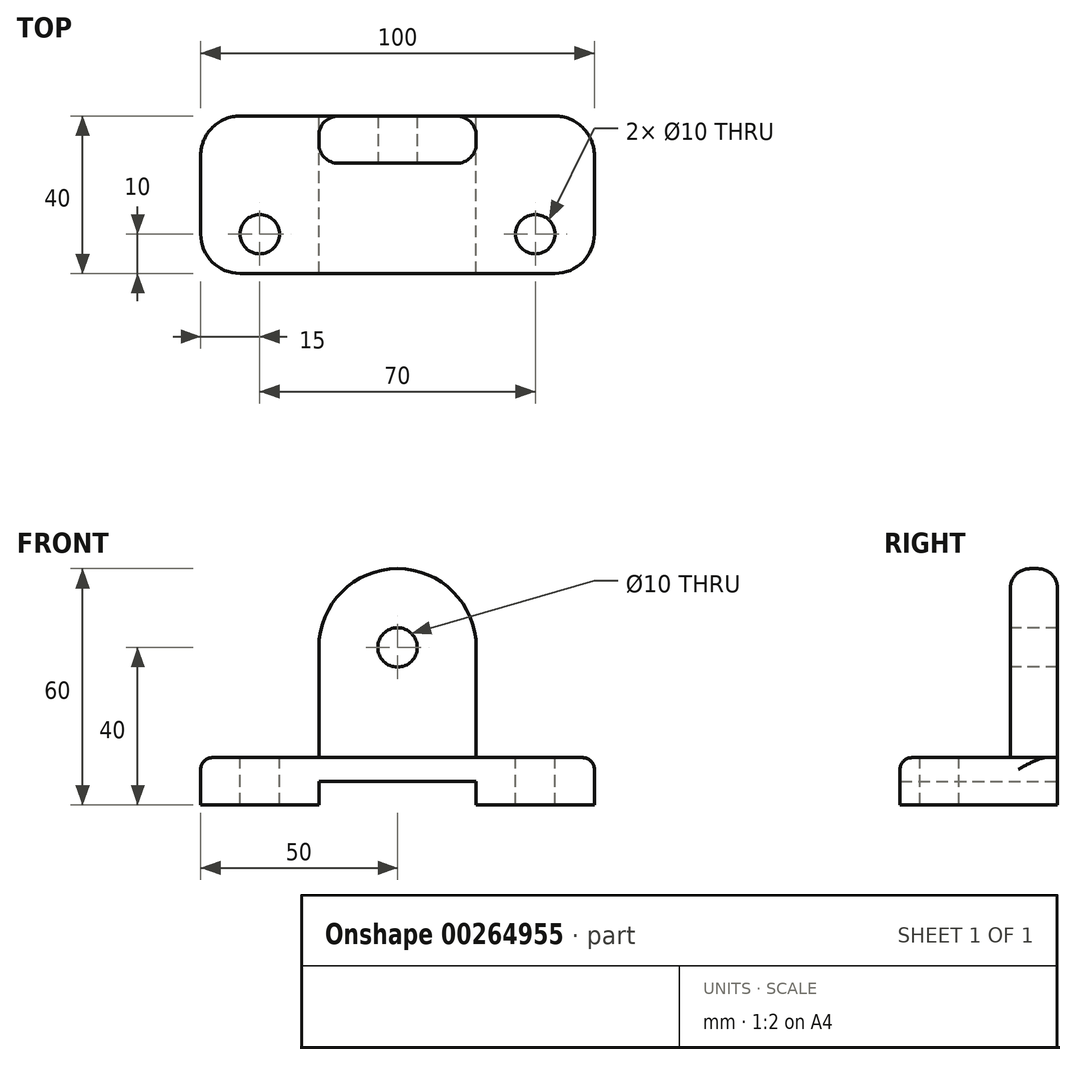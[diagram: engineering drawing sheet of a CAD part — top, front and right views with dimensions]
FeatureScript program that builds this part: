
annotation { "Feature Type Name" : "Feature", "Feature Type Description" : "" }
export const myFeature = defineFeature(function(context is Context, id is Id, definition is map)
    precondition{}
    {
        {
            var Q0;
            Q0=qCreatedBy(makeId("Top.planeOp"),FACE);
            var sketch = newSketch(context, id + "F0", { "sketchPlane" : qUnion([Q0])});
            skLineSegment(sketch, "E0.bottom", {"start": v(40, 20) * mm, "end": v(-40, 20) * mm});
            skLineSegment(sketch, "E0.top", {"start": v(40, -20) * mm, "end": v(-40, -20) * mm});
            skLineSegment(sketch, "E0.left", {"start": v(50, 10) * mm, "end": v(50, -10) * mm});
            skLineSegment(sketch, "E0.right", {"start": v(-50, 10) * mm, "end": v(-50, -10) * mm});
            skPoint(sketch, "E0.middle", {"position": v(0, 0) * mm});
            skPoint(sketch, "E1.visualSharp", {"position": v(-50, 20) * mm});
            skArc(sketch, "E1.filletArc", {"start": v(-40, 20) * mm, "mid": v(-47.07, 17.07) * mm, "end": v(-50, 10) * mm});
            skPoint(sketch, "E2.visualSharp", {"position": v(-50, -20) * mm});
            skArc(sketch, "E2.filletArc", {"start": v(-50, -10) * mm, "mid": v(-47.07, -17.07) * mm, "end": v(-40, -20) * mm});
            skPoint(sketch, "E3.visualSharp", {"position": v(50, -20) * mm});
            skArc(sketch, "E3.filletArc", {"start": v(40, -20) * mm, "mid": v(47.07, -17.07) * mm, "end": v(50, -10) * mm});
            skPoint(sketch, "E4.visualSharp", {"position": v(50, 20) * mm});
            skArc(sketch, "E4.filletArc", {"start": v(50, 10) * mm, "mid": v(47.07, 17.07) * mm, "end": v(40, 20) * mm});
            skCircle(sketch, "E5", {"center": v(-35, 10) * mm, "radius": 5 * mm});
            skCircle(sketch, "E6.MirrorC", {"center": v(35, 10) * mm, "radius": 5 * mm});
            skSolve(sketch);
        }
        {
            var Q0;
            Q0 = qSketchRegion(id + "F0", true);
            extrude(context, id + "F1", {"entities" : qUnion([Q0]), "depth" : 12 * mm});
        }
        {
            var Q0;
            Q0=makeQuery(id+"F1.opExtrude","CAP_FACE",FACE,{"disambiguationData":[OSD([sQuery(id+"F0.wireOp",EDGE,"E0.bottom"),sQuery(id+"F0.wireOp",EDGE,"E0.top"),sQuery(id+"F0.wireOp",EDGE,"E0.left"),sQuery(id+"F0.wireOp",EDGE,"E0.right"),sQuery(id+"F0.wireOp",EDGE,"E1.filletArc"),sQuery(id+"F0.wireOp",EDGE,"E2.filletArc"),sQuery(id+"F0.wireOp",EDGE,"E3.filletArc"),sQuery(id+"F0.wireOp",EDGE,"E4.filletArc"),sQuery(id+"F0.wireOp",EDGE,"E5"),sQuery(id+"F0.wireOp",EDGE,"E6.MirrorC")])],"isStart":false});
            var sketch = newSketch(context, id + "F2", { "sketchPlane" : qUnion([Q0])});
            skLineSegment(sketch, "E7.bottom", {"start": v(20, 20) * mm, "end": v(-20, 20) * mm});
            skLineSegment(sketch, "E7.top", {"start": v(20, -20) * mm, "end": v(-20, -20) * mm});
            skLineSegment(sketch, "E7.left", {"start": v(20, 20) * mm, "end": v(20, -20) * mm});
            skLineSegment(sketch, "E7.right", {"start": v(-20, 20) * mm, "end": v(-20, -20) * mm});
            skPoint(sketch, "E7.middle", {"position": v(0, 0) * mm});
            skSolve(sketch);
        }
        {
            var Q0;
            Q0 = qSketchRegion(id + "F2", true);
            extrude(context, id + "F3", {"entities" : qUnion([Q0]), "operationType" : NewBodyOperationType.REMOVE, "oppositeDirection" : true, "depth" : 6 * mm});
        }
        {
            var Q0;
            Q0=makeQuery(id+"F1.opExtrude","SWEPT_FACE",FACE,{"disambiguationData":[OSD([sQuery(id+"F0.wireOp",EDGE,"E0.top")])]});
            var sketch = newSketch(context, id + "F4", { "sketchPlane" : qUnion([Q0])});
            skLineSegment(sketch, "E8.bottom", {"start": v(20, 0) * mm, "end": v(-20, 0) * mm});
            skLineSegment(sketch, "E8.top", {"start": v(20, -28) * mm, "end": v(-20, -28) * mm});
            skLineSegment(sketch, "E8.left", {"start": v(20, 0) * mm, "end": v(20, -28) * mm});
            skLineSegment(sketch, "E8.right", {"start": v(-20, 0) * mm, "end": v(-20, -28) * mm});
            skArc(sketch, "E9", {"start": v(20, -28) * mm, "mid": v(0, -48) * mm, "end": v(-20, -28) * mm});
            skSolve(sketch);
        }
        {
            var Q0;
            Q0 = qSketchRegion(id + "F4", true);
            extrude(context, id + "F5", {"entities" : qUnion([Q0]), "oppositeDirection" : true, "depth" : 12 * mm});
        }
        {
            var Q0;
            Q0=makeQuery(id+"F5.opExtrude","CAP_FACE",FACE,{"disambiguationData":[OSD([sQuery(id+"F4.wireOp",EDGE,"E8.bottom"),sQuery(id+"F4.wireOp",EDGE,"E8.left"),sQuery(id+"F4.wireOp",EDGE,"E8.right"),sQuery(id+"F4.wireOp",EDGE,"E9")])],"isStart":false});
            var sketch = newSketch(context, id + "F6", { "sketchPlane" : qUnion([Q0])});
            skCircle(sketch, "E10", {"center": v(0, -28) * mm, "radius": 5 * mm});
            skSolve(sketch);
        }
        {
            var Q0;
            Q0 = qSketchRegion(id + "F6", true);
            extrude(context, id + "F7", {"entities" : qUnion([Q0]), "operationType" : NewBodyOperationType.REMOVE, "endBound" : BoundingType.THROUGH_ALL, "oppositeDirection" : true, "depth" : 25 * mm});
        }
        {
            var Q0;
            Q0=makeQuery(id+"F1.opExtrude","CAP_EDGE",EDGE,{"disambiguationData":[OSD([sQuery(id+"F0.wireOp",EDGE,"E0.right")])],"isStart":true});
            var Q1;
            Q1=makeQuery(id+"F1.opExtrude","CAP_EDGE",EDGE,{"disambiguationData":[OSD([sQuery(id+"F0.wireOp",EDGE,"E0.bottom")])],"isStart":true});
            var Q2;
            Q2=makeQuery(id+"F1.opExtrude","CAP_EDGE",EDGE,{"disambiguationData":[OSD([sQuery(id+"F0.wireOp",EDGE,"E0.left")])],"isStart":true});
            fillet(context, id + "F8", {"entities" : qUnion([Q0, Q1, Q2]), "radius" : 3 * mm, "allowEdgeOverflow" : false});
        }
        {
            var Q0;
            Q0=makeQuery(id+"F5.opExtrude","CAP_EDGE",EDGE,{"disambiguationData":[OSD([sQuery(id+"F4.wireOp",EDGE,"E8.right")])],"isStart":false});
            var Q1;
            Q1=makeQuery(id+"F5.opExtrude","CAP_EDGE",EDGE,{"disambiguationData":[OSD([sQuery(id+"F4.wireOp",EDGE,"E9")])],"isStart":true});
            fillet(context, id + "F9", {"entities" : qUnion([Q0, Q1]), "radius" : 5 * mm, "tangentPropagation" : true, "allowEdgeOverflow" : false});
        }
        {
            var Q0;
            Q0=makeQuery(id+"F5.opExtrude","SWEPT_BODY",BODY,{"disambiguationData":[OSD([sQuery(id+"F4.wireOp",EDGE,"E8.bottom"),sQuery(id+"F4.wireOp",EDGE,"E8.left"),sQuery(id+"F4.wireOp",EDGE,"E8.right"),sQuery(id+"F4.wireOp",EDGE,"E9")])]});
            var Q1;
            Q1=makeQuery(id+"F1.opExtrude","SWEPT_BODY",BODY,{"disambiguationData":[OSD([sQuery(id+"F0.wireOp",EDGE,"E0.bottom"),sQuery(id+"F0.wireOp",EDGE,"E0.top"),sQuery(id+"F0.wireOp",EDGE,"E0.left"),sQuery(id+"F0.wireOp",EDGE,"E0.right"),sQuery(id+"F0.wireOp",EDGE,"E1.filletArc"),sQuery(id+"F0.wireOp",EDGE,"E2.filletArc"),sQuery(id+"F0.wireOp",EDGE,"E3.filletArc"),sQuery(id+"F0.wireOp",EDGE,"E4.filletArc"),sQuery(id+"F0.wireOp",EDGE,"E5"),sQuery(id+"F0.wireOp",EDGE,"E6.MirrorC")])]});
            var Q2;
            Q2=qCreatedBy(makeId("Top.planeOp"),FACE);
            mirror(context, id + "F10", {"entities" : qUnion([Q0, Q1]), "mirrorPlane" : qUnion([Q2])});
        }
        {
            var Q0;
            Q0=makeQuery(id+"F1.opExtrude","SWEPT_BODY",BODY,{"disambiguationData":[OSD([sQuery(id+"F0.wireOp",EDGE,"E0.bottom"),sQuery(id+"F0.wireOp",EDGE,"E0.top"),sQuery(id+"F0.wireOp",EDGE,"E0.left"),sQuery(id+"F0.wireOp",EDGE,"E0.right"),sQuery(id+"F0.wireOp",EDGE,"E1.filletArc"),sQuery(id+"F0.wireOp",EDGE,"E2.filletArc"),sQuery(id+"F0.wireOp",EDGE,"E3.filletArc"),sQuery(id+"F0.wireOp",EDGE,"E4.filletArc"),sQuery(id+"F0.wireOp",EDGE,"E5"),sQuery(id+"F0.wireOp",EDGE,"E6.MirrorC")])]});
            var Q1;
            Q1=makeQuery(id+"F5.opExtrude","SWEPT_BODY",BODY,{"disambiguationData":[OSD([sQuery(id+"F4.wireOp",EDGE,"E8.bottom"),sQuery(id+"F4.wireOp",EDGE,"E8.left"),sQuery(id+"F4.wireOp",EDGE,"E8.right"),sQuery(id+"F4.wireOp",EDGE,"E9")])]});
            deleteBodies(context, id + "F11", {"entities" : qUnion([Q0, Q1])});
        }
        {
            var Q0;
            Q0=makeQuery(id+"F10.opPattern","COPY",BODY,{"derivedFrom":makeQuery(id+"F5.opExtrude","SWEPT_BODY",BODY,{"disambiguationData":[OSD([sQuery(id+"F4.wireOp",EDGE,"E8.bottom"),sQuery(id+"F4.wireOp",EDGE,"E8.left"),sQuery(id+"F4.wireOp",EDGE,"E8.right"),sQuery(id+"F4.wireOp",EDGE,"E9")])]}),"instanceName":"1"});
            var Q1;
            Q1=makeQuery(id+"F10.opPattern","COPY",BODY,{"derivedFrom":makeQuery(id+"F1.opExtrude","SWEPT_BODY",BODY,{"disambiguationData":[OSD([sQuery(id+"F0.wireOp",EDGE,"E0.bottom"),sQuery(id+"F0.wireOp",EDGE,"E0.top"),sQuery(id+"F0.wireOp",EDGE,"E0.left"),sQuery(id+"F0.wireOp",EDGE,"E0.right"),sQuery(id+"F0.wireOp",EDGE,"E1.filletArc"),sQuery(id+"F0.wireOp",EDGE,"E2.filletArc"),sQuery(id+"F0.wireOp",EDGE,"E3.filletArc"),sQuery(id+"F0.wireOp",EDGE,"E4.filletArc"),sQuery(id+"F0.wireOp",EDGE,"E5"),sQuery(id+"F0.wireOp",EDGE,"E6.MirrorC")])]}),"instanceName":"1"});
            var Q2;
            Q2=qCreatedBy(makeId("Front.planeOp"),FACE);
            mirror(context, id + "F12", {"entities" : qUnion([Q0, Q1]), "mirrorPlane" : qUnion([Q2])});
        }
        {
            var Q0;
            Q0=makeQuery(id+"F10.opPattern","COPY",BODY,{"derivedFrom":makeQuery(id+"F5.opExtrude","SWEPT_BODY",BODY,{"disambiguationData":[OSD([sQuery(id+"F4.wireOp",EDGE,"E8.bottom"),sQuery(id+"F4.wireOp",EDGE,"E8.left"),sQuery(id+"F4.wireOp",EDGE,"E8.right"),sQuery(id+"F4.wireOp",EDGE,"E9")])]}),"instanceName":"1"});
            var Q1;
            Q1=makeQuery(id+"F10.opPattern","COPY",BODY,{"derivedFrom":makeQuery(id+"F1.opExtrude","SWEPT_BODY",BODY,{"disambiguationData":[OSD([sQuery(id+"F0.wireOp",EDGE,"E0.bottom"),sQuery(id+"F0.wireOp",EDGE,"E0.top"),sQuery(id+"F0.wireOp",EDGE,"E0.left"),sQuery(id+"F0.wireOp",EDGE,"E0.right"),sQuery(id+"F0.wireOp",EDGE,"E1.filletArc"),sQuery(id+"F0.wireOp",EDGE,"E2.filletArc"),sQuery(id+"F0.wireOp",EDGE,"E3.filletArc"),sQuery(id+"F0.wireOp",EDGE,"E4.filletArc"),sQuery(id+"F0.wireOp",EDGE,"E5"),sQuery(id+"F0.wireOp",EDGE,"E6.MirrorC")])]}),"instanceName":"1"});
            deleteBodies(context, id + "F13", {"entities" : qUnion([Q0, Q1])});
        }
    });
